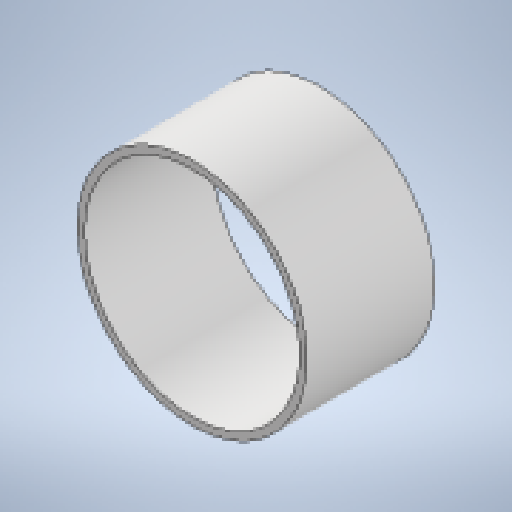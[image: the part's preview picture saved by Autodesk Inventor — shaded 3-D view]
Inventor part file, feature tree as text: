
AUTODESK INVENTOR PART (.ipt)
format: ipt  version: 2025.1 (Build 291241020, 241B)  size: 146,432 bytes
history: native  units: mm
features: extrude x1, sketch x1
ambient origin geometry x8: Origin, YZ Plane, XZ Plane, XY Plane, X Axis, Y Axis, Z Axis, Center Point
bodies: Solid1 (feature_tree)
feature tree (2):
  extrude  "Extrusion1"  Depth=50.0mm
  sketch  "Sketch1"  dims[d0=90.0mm d1=3.0mm d2=50.0mm d3=0.0mm]
